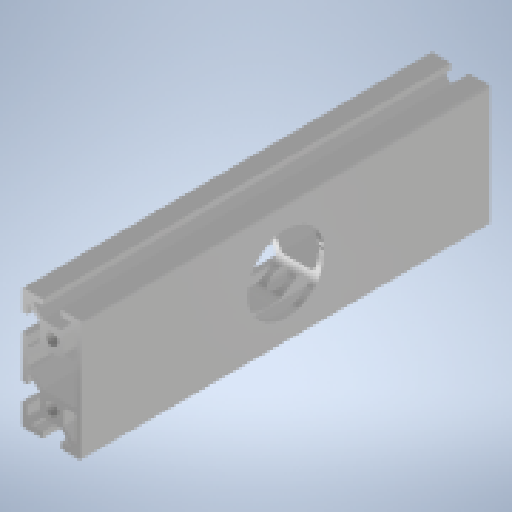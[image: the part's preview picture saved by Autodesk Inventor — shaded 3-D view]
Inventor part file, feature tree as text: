
AUTODESK INVENTOR PART (.ipt)
format: ipt  version: 2024 (Build 280153000, 153)  size: 365,568 bytes
history: native  units: mm
features: other x7, thread x4, sketch x3, hole x2, extrude x1, pattern_linear x1
ambient origin geometry x8: Origin, YZ Plane, XZ Plane, XY Plane, X Axis, Y Axis, Z Axis, Center Point
bodies: Solid1 (feature_tree)
feature tree (18):
  extrude  "Extrusion1"  Depth=10.0mm TaperAngle=0.0deg
  hole  "Hole1"  [1 undecoded]
  pattern_linear  "Rectangular Pattern1"  Spacing1=10.0mm  [1 undecoded]
  other  "C1_XY"
  other  "C1_YZ"
  other  "C1_ZX"
  other  "C1_X"
  other  "C1_Y"
  other  "C1_Z"
  other  "C1_Center"
  thread  "Thread1"  [1 undecoded]
  thread  "Thread2"  [1 undecoded]
  thread  "Thread3"  [1 undecoded]
  thread  "Thread4"  [1 undecoded]
  hole  "Hole2"  [1 undecoded]
  sketch  "Sketch_63"  dims[d15=0.0mm d16=10.0mm d17=0.0mm d18=10.0mm d19=0.0mm d20=10.0mm d21=0.0mm d22=10.0mm d23=0.0mm d24=25.4mm d25=6.0mm d26=4.0mm d27=2.0mm d28=90.0deg d29=8.0mm d30=20.594885mm]
  sketch  "Sketch2"  dims[d0=135.2mm d1=0.0mm]
  sketch  "Sketch3"  dims[d2=4.2mm d3=6.0mm d4=4.0mm d5=2.0mm d6=90.0deg d7=138.0mm d8=0.0mm d9=20.0mm d11=20.0mm d12=10.0mm d14=0.0mm]
note: 7 required parameter values undecoded (feature->parameter linkage not recoverable at this tier; creation-order binding heuristic only, values carry confidence <= 0.55)
